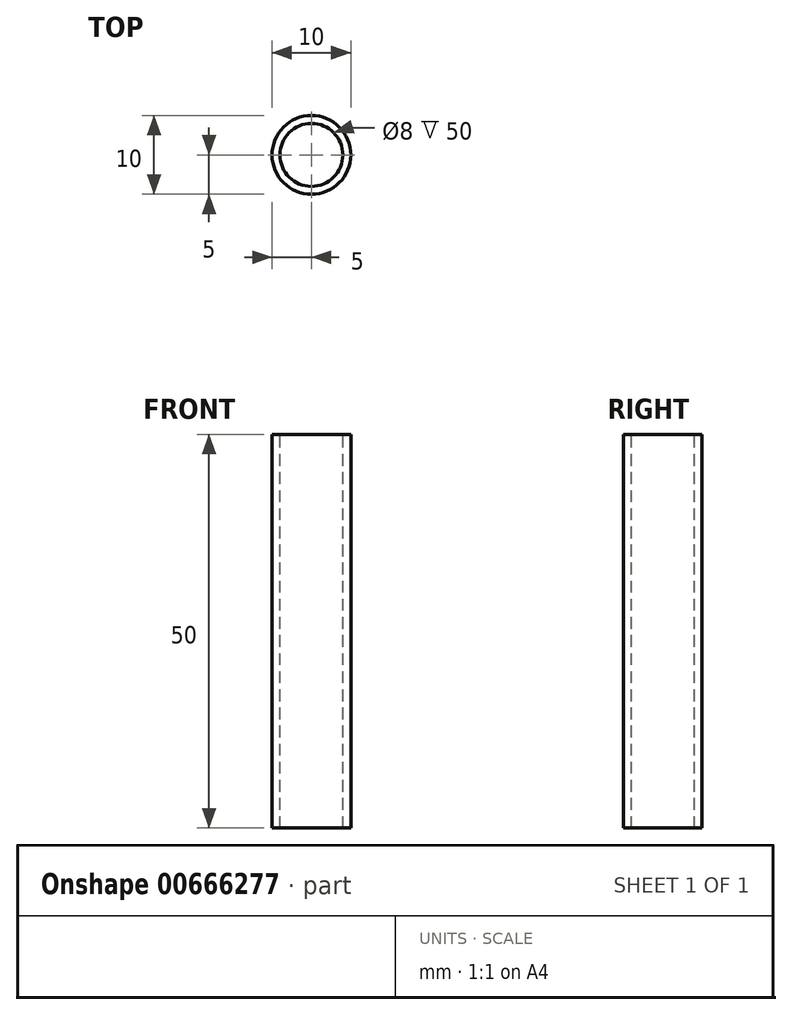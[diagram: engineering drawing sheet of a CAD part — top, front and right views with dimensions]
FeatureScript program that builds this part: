
annotation { "Feature Type Name" : "Feature", "Feature Type Description" : "" }
export const myFeature = defineFeature(function(context is Context, id is Id, definition is map)
    precondition{}
    {
        {
            var Q0;
            Q0=qCreatedBy(makeId("Front.planeOp"),FACE);
            var sketch = newSketch(context, id + "F0", { "sketchPlane" : qUnion([Q0])});
            skLineSegment(sketch, "E0", {"start": v(0, 0) * mm, "end": v(0, 50) * mm});
            skSolve(sketch);
        }
        {
            var Q0;
            Q0=qCreatedBy(makeId("Top.planeOp"),FACE);
            var sketch = newSketch(context, id + "F1", { "sketchPlane" : qUnion([Q0])});
            skCircle(sketch, "E1", {"center": v(0, 0) * mm, "radius": 4 * mm});
            skCircle(sketch, "E2", {"center": v(0, 0) * mm, "radius": 5 * mm});
            skSolve(sketch);
        }
        {
            var Q0;
            Q0=makeQuery(id+"F1.imprint","IMPRINT",FACE,{"disambiguationData":[TD([[makeQuery(id+"F1.imprint","IMPRINT",EDGE,{"derivedFrom":sQuery(id+"F1.wireOp",EDGE,"E1")}),-1.0]])]});
            var Q1;
            Q1=sQuery(id+"F0.wireOp",EDGE,"E0");
            var Q2;
            Q2=sQuery(id+"F0.wireOp",EDGE,"CCExxTKh-58sI-6QzY-uNXw-khPFwXC8bCQZ");
            var Q3;
            Q3=sQuery(id+"F0.wireOp",EDGE,"ZPpe7haA-fSdd-dvkM-u7Oe-NqCRAf2rkXxO");
            sweep(context, id + "F2", {"profiles" : qUnion([Q0]), "path" : qUnion([Q1, Q2, Q3])});
        }
    });
